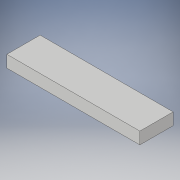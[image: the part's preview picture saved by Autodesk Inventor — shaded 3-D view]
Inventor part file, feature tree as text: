
AUTODESK INVENTOR PART (.ipt)
format: ipt  version: 2018 (Build 220112000, 112)  size: 89,600 bytes
history: native  units: in
note: dims shown in document units (in); Inventor stores cm internally (conversion verified against a paired STEP export)
features: extrude x1, sketch x1
ambient origin geometry x8: Origin, YZ Plane, XZ Plane, XY Plane, X Axis, Y Axis, Z Axis, Center Point
bodies: Solid1 (feature_tree)
feature tree (2):
  extrude  "Extrusion1"  Depth=1.9685in
  sketch  "Sketch1"  dims[d0=7.874in d1=1.9685in d2=0.7087in d3=0.0in]
